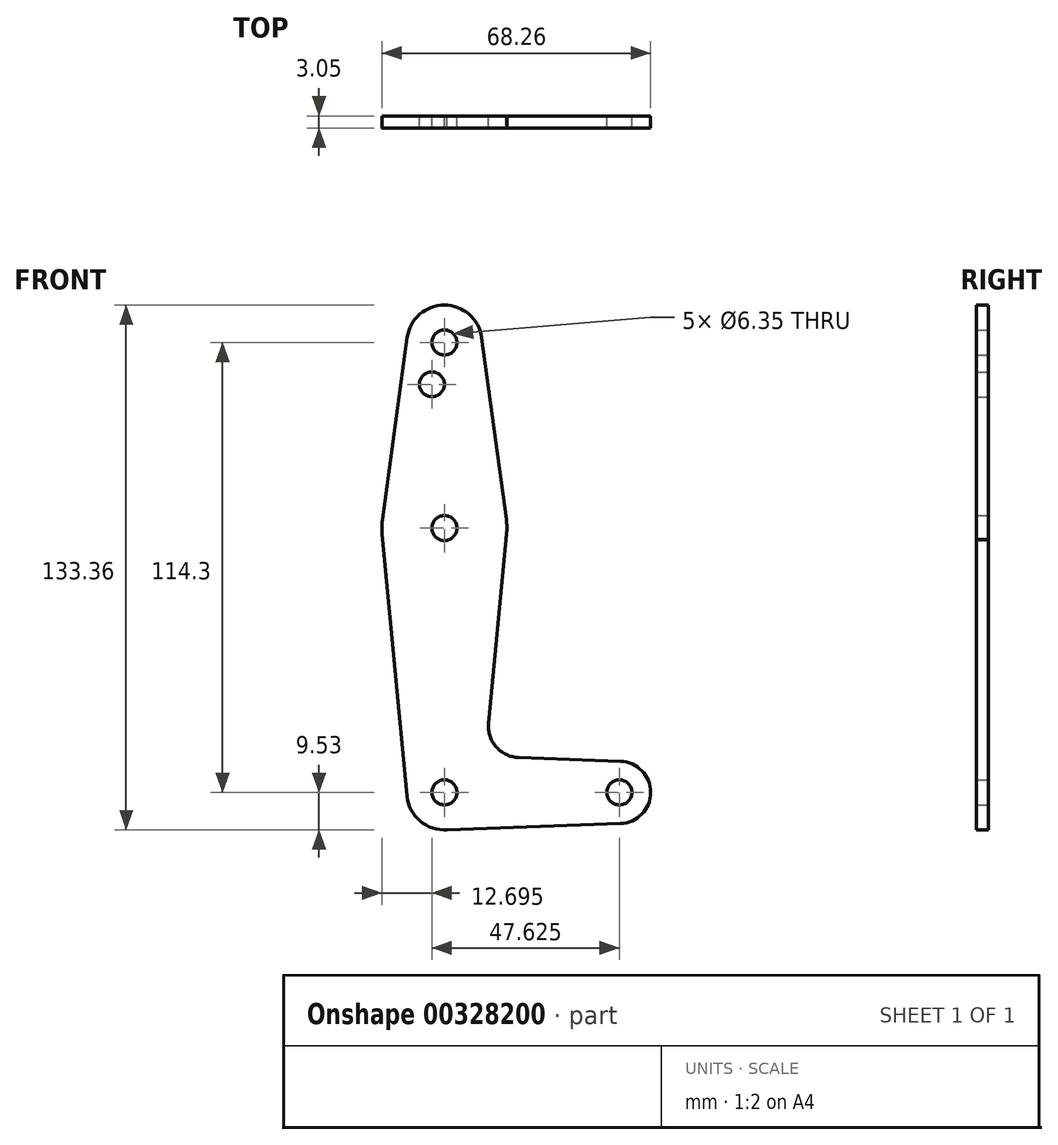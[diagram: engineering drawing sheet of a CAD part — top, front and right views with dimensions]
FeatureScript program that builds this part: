
annotation { "Feature Type Name" : "Feature", "Feature Type Description" : "" }
export const myFeature = defineFeature(function(context is Context, id is Id, definition is map)
    precondition{}
    {
        {
            var Q0;
            Q0=qCreatedBy(makeId("Front.planeOp"),FACE);
            var sketch = newSketch(context, id + "F0", { "sketchPlane" : qUnion([Q0])});
            skLineSegment(sketch, "E0", {"start": v(0, 0) * mm, "end": v(44.45, 0) * mm, "construction": true});
            skCircle(sketch, "E1", {"center": v(0, 0) * mm, "radius": 9.53 * mm});
            skCircle(sketch, "E2", {"center": v(44.45, 0) * mm, "radius": 7.94 * mm});
            skLineSegment(sketch, "E3", {"start": v(18.85, 8.86) * mm, "end": v(44.73, 7.93) * mm});
            skLineSegment(sketch, "E4", {"start": v(0, -9.53) * mm, "end": v(44.73, -7.93) * mm});
            skCircle(sketch, "E5", {"center": v(0, 0) * mm, "radius": 3.18 * mm});
            skCircle(sketch, "E6", {"center": v(44.45, 0) * mm, "radius": 3.18 * mm});
            skLineSegment(sketch, "E7", {"start": v(0, 0) * mm, "end": v(0, 114.3) * mm, "construction": true});
            skCircle(sketch, "E8", {"center": v(0, 67.16) * mm, "radius": 15.88 * mm});
            skCircle(sketch, "E9", {"center": v(0, 114.3) * mm, "radius": 9.53 * mm});
            skLineSegment(sketch, "E10", {"start": v(-9.44, 115.58) * mm, "end": v(-15.73, 69.3) * mm});
            skLineSegment(sketch, "E11", {"start": v(9.44, 115.58) * mm, "end": v(15.73, 69.3) * mm});
            skLineSegment(sketch, "E12", {"start": v(15.88, 67.16) * mm, "end": v(11.21, 17.55) * mm});
            skCircle(sketch, "E13", {"center": v(0, 114.3) * mm, "radius": 3.18 * mm});
            skCircle(sketch, "E14", {"center": v(0, 67.16) * mm, "radius": 3.18 * mm});
            skCircle(sketch, "E15", {"center": v(-3.18, 103.69) * mm, "radius": 3.18 * mm});
            skPoint(sketch, "E16.newPointA", {"position": v(9.57, 0) * mm});
            skArc(sketch, "E16.filletArc", {"start": v(11.21, 17.55) * mm, "mid": v(13.16, 11.56) * mm, "end": v(18.85, 8.86) * mm});
            skLineSegment(sketch, "E17", {"start": v(-15.8, 65.66) * mm, "end": v(-9.48, -0.9) * mm});
            skSolve(sketch);
        }
        {
            var Q0;
            Q0 = qSketchRegion(id + "F0", true);
            extrude(context, id + "F1", {"entities" : qUnion([Q0]), "depth" : 3.05 * mm});
        }
    });
